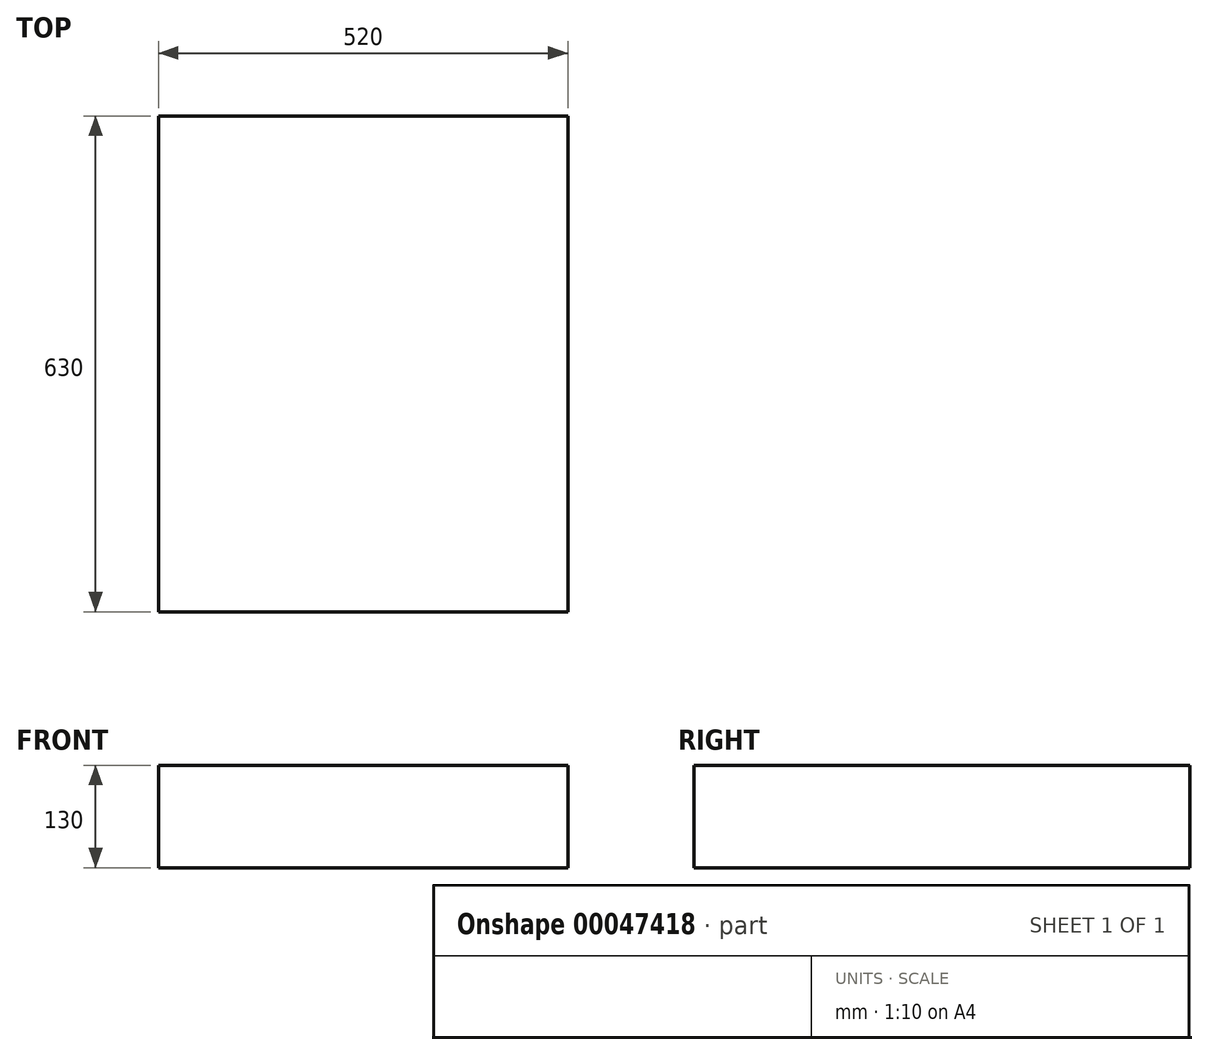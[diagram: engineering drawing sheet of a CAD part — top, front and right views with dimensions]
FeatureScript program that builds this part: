
annotation { "Feature Type Name" : "Feature", "Feature Type Description" : "" }
export const myFeature = defineFeature(function(context is Context, id is Id, definition is map)
    precondition{}
    {
        {
            var Q0;
            Q0=qCreatedBy(makeId("Top.planeOp"),FACE);
            var sketch = newSketch(context, id + "F0", { "sketchPlane" : qUnion([Q0])});
            skLineSegment(sketch, "E0.rect.bottom", {"start": v(315, 260) * mm, "end": v(-315, 260) * mm});
            skLineSegment(sketch, "E0.rect.top", {"start": v(315, -260) * mm, "end": v(-315, -260) * mm});
            skLineSegment(sketch, "E0.rect.left", {"start": v(315, 260) * mm, "end": v(315, -260) * mm});
            skLineSegment(sketch, "E0.rect.right", {"start": v(-315, 260) * mm, "end": v(-315, -260) * mm});
            skPoint(sketch, "E0.rect.middle", {"position": v(0, 0) * mm});
            skSolve(sketch);
        }
        {
            var Q0;
            Q0 = qSketchRegion(id + "F0", true);
            extrude(context, id + "F1", {"entities" : qUnion([Q0]), "depth" : 130 * mm});
        }
        {
            var Q0;
            Q0=makeQuery(id+"F1.opExtrude","SWEPT_BODY",BODY,{"disambiguationData":[OSD([sQuery(id+"F0.wireOp",EDGE,"E0.rect.bottom"),sQuery(id+"F0.wireOp",EDGE,"E0.rect.top"),sQuery(id+"F0.wireOp",EDGE,"E0.rect.left"),sQuery(id+"F0.wireOp",EDGE,"E0.rect.right")])]});
            var Q1;
            Q1=makeQuery(id+"F1.opExtrude","SWEPT_EDGE",EDGE,{"disambiguationData":[OSD([sQuery(id+"F0.wireOp",EDGE,"E0.rect.bottom"),sQuery(id+"F0.wireOp",EDGE,"E0.rect.left")])]});
            transform(context, id + "F2", {"entities" : qUnion([Q0]), "transformType" : TransformType.ROTATION, "transformAxis" : qUnion([Q1]), "angle" : 90 * degree, "makeCopy" : false});
        }
    });
